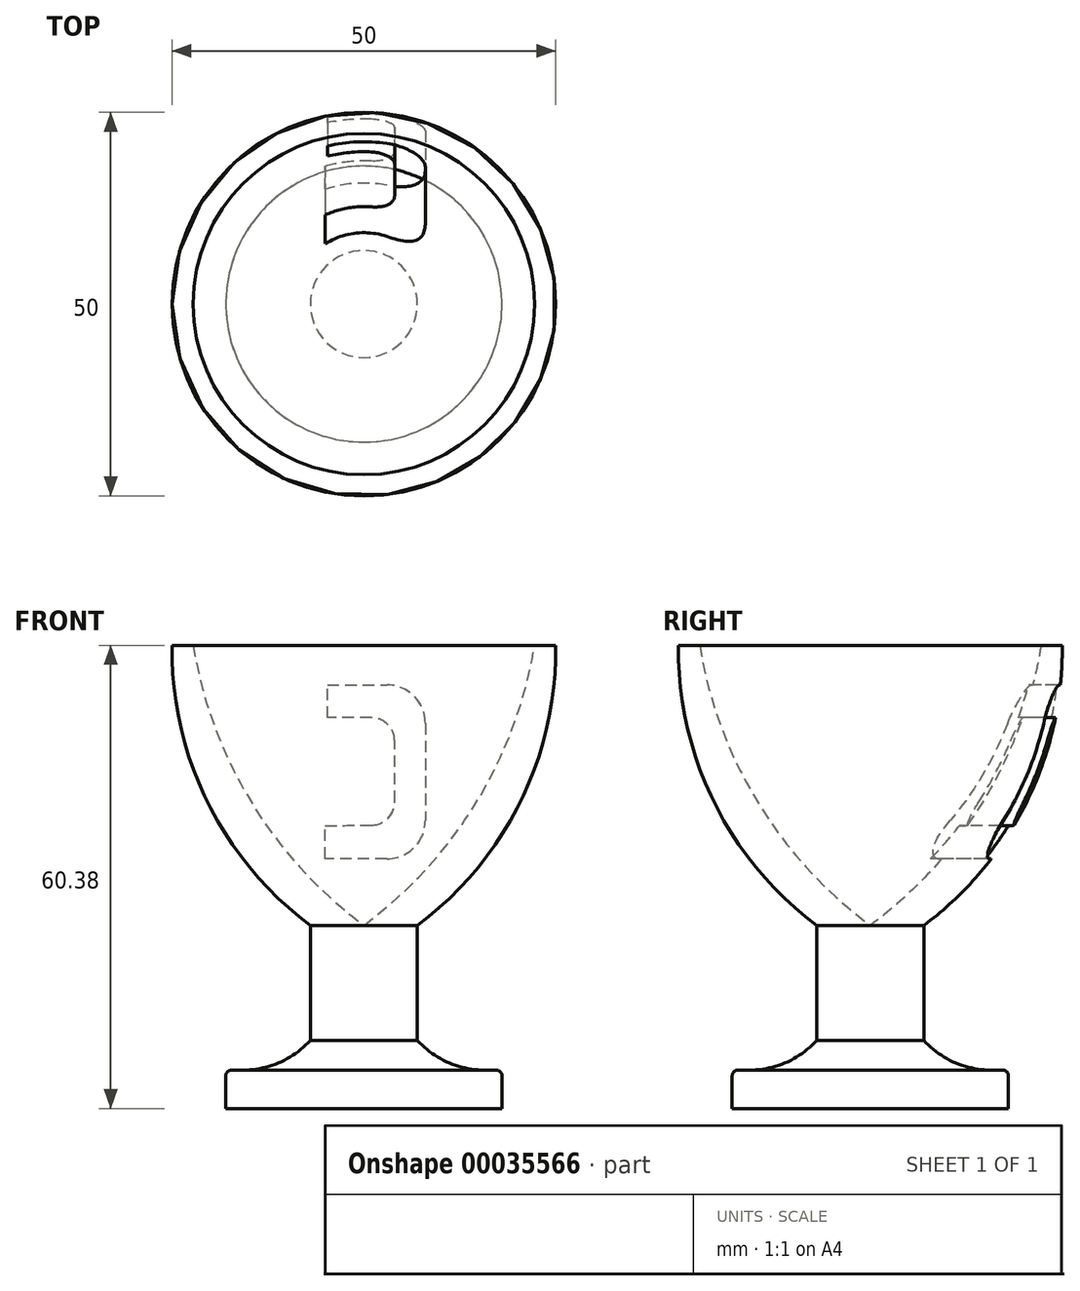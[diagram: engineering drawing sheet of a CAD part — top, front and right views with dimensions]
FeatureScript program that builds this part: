
annotation { "Feature Type Name" : "Feature", "Feature Type Description" : "" }
export const myFeature = defineFeature(function(context is Context, id is Id, definition is map)
    precondition{}
    {
        {
            var Q0;
            Q0=qCreatedBy(makeId("Front.planeOp"),FACE);
            var sketch = newSketch(context, id + "F0", { "sketchPlane" : qUnion([Q0])});
            skLineSegment(sketch, "E0", {"start": v(0, 0) * mm, "end": v(-18, 0) * mm});
            skLineSegment(sketch, "E1", {"start": v(-18, 0) * mm, "end": v(-18, 4.25) * mm});
            skLineSegment(sketch, "E2", {"start": v(-17.25, 5) * mm, "end": v(-15.75, 5) * mm});
            skPoint(sketch, "E3.visualSharp", {"position": v(-18, 5) * mm});
            skArc(sketch, "E3.filletArc", {"start": v(-17.25, 5) * mm, "mid": v(-17.78, 4.78) * mm, "end": v(-18, 4.25) * mm});
            skArc(sketch, "E4", {"start": v(-15.75, 5) * mm, "mid": v(-10.95, 6.01) * mm, "end": v(-6.98, 8.88) * mm});
            skLineSegment(sketch, "E5", {"start": v(-6.98, 8.88) * mm, "end": v(-6.98, 23.88) * mm});
            skArc(sketch, "E6", {"start": v(-25, 60.38) * mm, "mid": v(-20.37, 39.96) * mm, "end": v(-6.98, 23.88) * mm});
            skLineSegment(sketch, "E7", {"start": v(0, 0) * mm, "end": v(0, 23.88) * mm});
            skLineSegment(sketch, "E8", {"start": v(-25, 60.38) * mm, "end": v(-22.25, 60.38) * mm});
            skArc(sketch, "E9", {"start": v(-22.25, 60.38) * mm, "mid": v(-14.69, 39.96) * mm, "end": v(0, 23.88) * mm});
            skSolve(sketch);
        }
        {
            var Q0;
            Q0 = qSketchRegion(id + "F0", true);
            var Q1;
            Q1=sQuery(id+"F0.wireOp",EDGE,"E7");
            revolve(context, id + "F1", {"entities" : qUnion([Q0]), "axis" : qUnion([Q1]), "revolveType" : RevolveType.FULL});
        }
        {
            var Q0;
            Q0=qCreatedBy(makeId("Front.planeOp"),FACE);
            var sketch = newSketch(context, id + "F2", { "sketchPlane" : qUnion([Q0])});
            skLineSegment(sketch, "E10", {"start": v(-4.74, 55.23) * mm, "end": v(3, 55.23) * mm});
            skLineSegment(sketch, "E11", {"start": v(8, 50.23) * mm, "end": v(8, 37.55) * mm});
            skLineSegment(sketch, "E12", {"start": v(2.99, 32.55) * mm, "end": v(-5.05, 32.58) * mm});
            skLineSegment(sketch, "E13", {"start": v(-5.05, 32.58) * mm, "end": v(-5.05, 36.87) * mm});
            skLineSegment(sketch, "E14", {"start": v(-5.05, 36.87) * mm, "end": v(1.03, 36.94) * mm});
            skLineSegment(sketch, "E15", {"start": v(4, 39.94) * mm, "end": v(4, 47.94) * mm});
            skLineSegment(sketch, "E16", {"start": v(1, 50.94) * mm, "end": v(-4.74, 50.94) * mm});
            skLineSegment(sketch, "E17", {"start": v(-4.74, 50.94) * mm, "end": v(-4.74, 55.23) * mm});
            skPoint(sketch, "E18.visualSharp", {"position": v(4, 36.97) * mm});
            skArc(sketch, "E18.filletArc", {"start": v(1.03, 36.94) * mm, "mid": v(3.13, 37.83) * mm, "end": v(4, 39.94) * mm});
            skPoint(sketch, "E19.visualSharp", {"position": v(4, 50.94) * mm});
            skArc(sketch, "E19.filletArc", {"start": v(4, 47.94) * mm, "mid": v(3.12, 50.06) * mm, "end": v(1, 50.94) * mm});
            skPoint(sketch, "E20.visualSharp", {"position": v(8, 32.54) * mm});
            skArc(sketch, "E20.filletArc", {"start": v(2.99, 32.55) * mm, "mid": v(6.53, 34.01) * mm, "end": v(8, 37.55) * mm});
            skPoint(sketch, "E21.visualSharp", {"position": v(8, 55.23) * mm});
            skArc(sketch, "E21.filletArc", {"start": v(8, 50.23) * mm, "mid": v(6.54, 53.77) * mm, "end": v(3, 55.23) * mm});
            skLineSegment(sketch, "E22", {"start": v(0, 50.77) * mm, "end": v(0, 37.1) * mm, "construction": true});
            skSolve(sketch);
        }
        {
            var Q0;
            Q0 = qSketchRegion(id + "F2", true);
            extrude(context, id + "F3", {"entities" : qUnion([Q0]), "operationType" : NewBodyOperationType.REMOVE, "endBound" : BoundingType.THROUGH_ALL, "oppositeDirection" : true, "depth" : 25 * mm});
        }
    });
